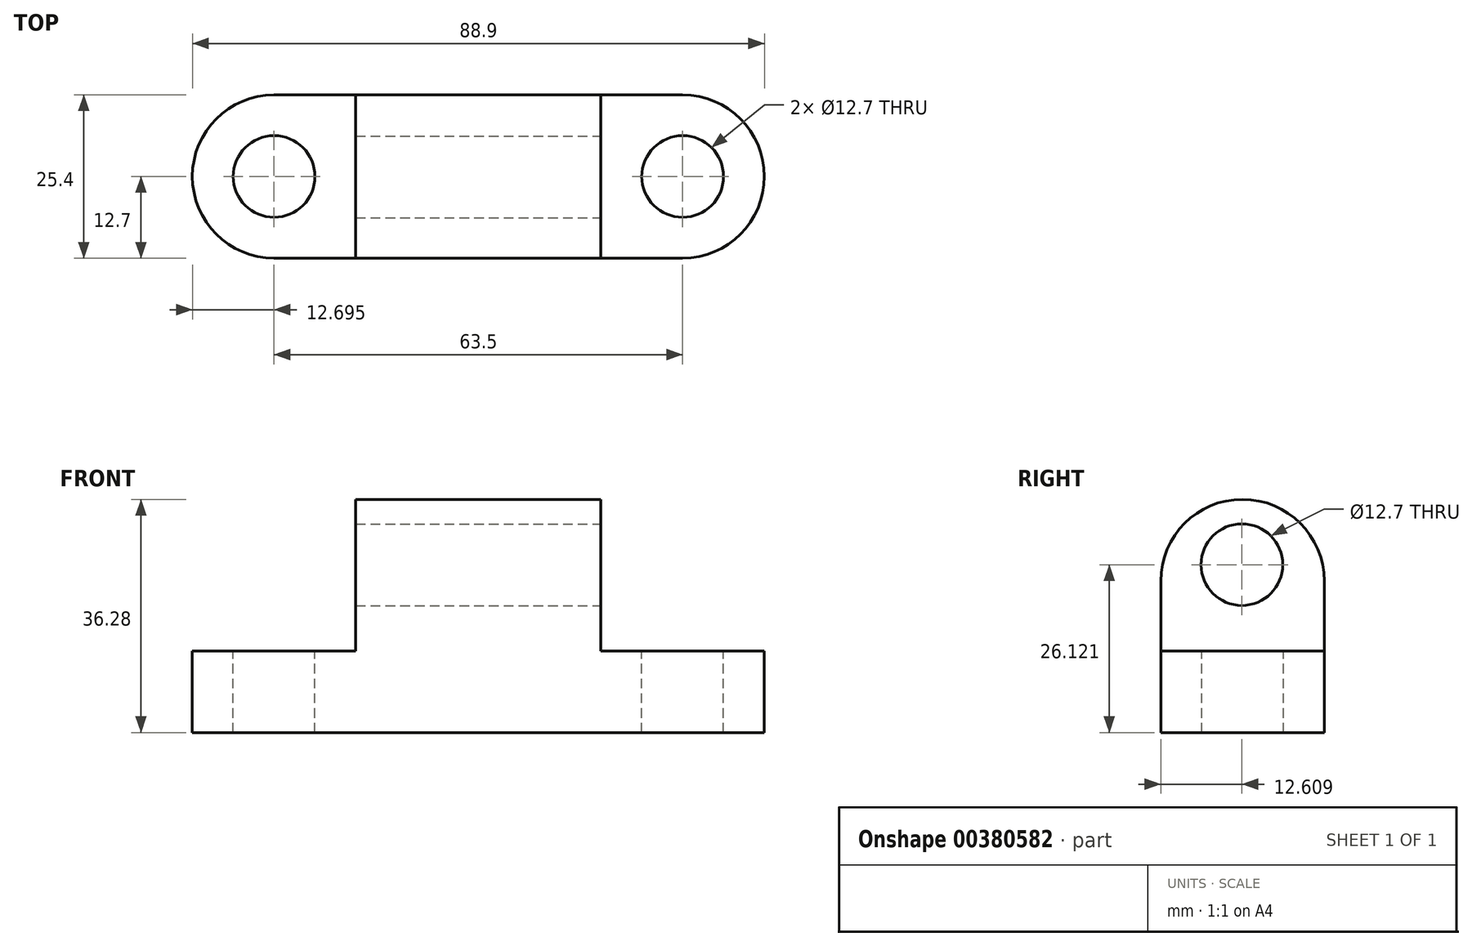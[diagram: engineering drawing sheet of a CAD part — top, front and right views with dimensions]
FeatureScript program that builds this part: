
annotation { "Feature Type Name" : "Feature", "Feature Type Description" : "" }
export const myFeature = defineFeature(function(context is Context, id is Id, definition is map)
    precondition{}
    {
        {
            var Q0;
            Q0=qCreatedBy(makeId("Front.planeOp"),FACE);
            var sketch = newSketch(context, id + "F0", { "sketchPlane" : qUnion([Q0])});
            skLineSegment(sketch, "E0", {"start": v(-50.93, 0) * mm, "end": v(-50.93, 12.7) * mm});
            skLineSegment(sketch, "E1", {"start": v(-50.93, 12.7) * mm, "end": v(-25.53, 12.7) * mm});
            skLineSegment(sketch, "E2", {"start": v(-25.53, 12.7) * mm, "end": v(-25.53, 36.28) * mm});
            skLineSegment(sketch, "E3", {"start": v(-25.53, 36.28) * mm, "end": v(12.57, 36.28) * mm});
            skLineSegment(sketch, "E4", {"start": v(12.57, 36.28) * mm, "end": v(12.57, 12.7) * mm});
            skLineSegment(sketch, "E5", {"start": v(12.57, 12.7) * mm, "end": v(37.97, 12.7) * mm});
            skLineSegment(sketch, "E6", {"start": v(37.97, 12.7) * mm, "end": v(37.97, 0) * mm});
            skLineSegment(sketch, "E7", {"start": v(37.97, 0) * mm, "end": v(-50.93, 0) * mm});
            skSolve(sketch);
        }
        {
            var Q0;
            Q0=makeQuery(id+"F0.imprint","IMPRINT",FACE,{"disambiguationData":[TD([[makeQuery(id+"F0.imprint","IMPRINT",EDGE,{"derivedFrom":sQuery(id+"F0.wireOp",EDGE,"E0")}),-1.0]])]});
            extrude(context, id + "F1", {"entities" : qUnion([Q0]), "depth" : 25.4 * mm});
        }
        {
            var Q0;
            Q0=makeQuery(id+"F1.opExtrude","SWEPT_FACE",FACE,{"disambiguationData":[OSD([sQuery(id+"F0.wireOp",EDGE,"E1")])]});
            var sketch = newSketch(context, id + "F2", { "sketchPlane" : qUnion([Q0])});
            skCircle(sketch, "E8", {"center": v(-38.23, -12.7) * mm, "radius": 12.7 * mm});
            skSolve(sketch);
        }
        {
            var Q0;
            {var subQ0=sQuery(id+"F2.wireOp",EDGE,"E8");var subQ1=sQuery(id+"F0.wireOp",EDGE,"E1");var subQ2=makeQuery(id+"F1.opExtrude","CAP_EDGE",EDGE,{"disambiguationData":[OSD([subQ1])],"isStart":true});var subQ3=makeQuery(id+"F2.imprint","INTERSECT",VERTEX,{"derivedFrom":[subQ2,subQ0]});Q0=makeQuery(id+"F2.imprint","IMPRINT",FACE,{"disambiguationData":[TD([[makeQuery(id+"F2.imprint","IMPRINT",EDGE,{"disambiguationData":[TD([[subQ3,-1.0]])],"derivedFrom":subQ0}),-1.0]])]});}
            var Q1;
            {var subQ0=sQuery(id+"F2.wireOp",EDGE,"E8");var subQ1=sQuery(id+"F0.wireOp",EDGE,"E1");var subQ4=makeQuery(id+"F1.opExtrude","CAP_EDGE",EDGE,{"disambiguationData":[OSD([subQ1])],"isStart":false});var subQ5=makeQuery(id+"F2.imprint","INTERSECT",VERTEX,{"derivedFrom":[subQ4,subQ0]});Q1=makeQuery(id+"F2.imprint","IMPRINT",FACE,{"disambiguationData":[TD([[makeQuery(id+"F2.imprint","IMPRINT",EDGE,{"disambiguationData":[TD([[subQ5,1.0]])],"derivedFrom":subQ0}),-1.0]])]});}
            extrude(context, id + "F3", {"entities" : qUnion([Q0, Q1]), "operationType" : NewBodyOperationType.REMOVE, "oppositeDirection" : true, "depth" : 25.4 * mm});
        }
        {
            var Q0;
            Q0=makeQuery(id+"F1.opExtrude","SWEPT_FACE",FACE,{"disambiguationData":[OSD([sQuery(id+"F0.wireOp",EDGE,"E5")])]});
            var sketch = newSketch(context, id + "F4", { "sketchPlane" : qUnion([Q0])});
            skCircle(sketch, "E9", {"center": v(25.27, -12.7) * mm, "radius": 12.7 * mm});
            skSolve(sketch);
        }
        {
            var Q0;
            {var subQ0=sQuery(id+"F4.wireOp",EDGE,"E9");var subQ1=sQuery(id+"F0.wireOp",EDGE,"E5");var subQ2=makeQuery(id+"F1.opExtrude","CAP_EDGE",EDGE,{"disambiguationData":[OSD([subQ1])],"isStart":true});var subQ3=makeQuery(id+"F4.imprint","INTERSECT",VERTEX,{"derivedFrom":[subQ2,subQ0]});Q0=makeQuery(id+"F4.imprint","IMPRINT",FACE,{"disambiguationData":[TD([[makeQuery(id+"F4.imprint","IMPRINT",EDGE,{"disambiguationData":[TD([[subQ3,1.0]])],"derivedFrom":subQ0}),-1.0]])]});}
            var Q1;
            {var subQ0=sQuery(id+"F4.wireOp",EDGE,"E9");var subQ1=sQuery(id+"F0.wireOp",EDGE,"E5");var subQ4=makeQuery(id+"F1.opExtrude","CAP_EDGE",EDGE,{"disambiguationData":[OSD([subQ1])],"isStart":false});var subQ5=makeQuery(id+"F4.imprint","INTERSECT",VERTEX,{"derivedFrom":[subQ4,subQ0]});Q1=makeQuery(id+"F4.imprint","IMPRINT",FACE,{"disambiguationData":[TD([[makeQuery(id+"F4.imprint","IMPRINT",EDGE,{"disambiguationData":[TD([[subQ5,-1.0]])],"derivedFrom":subQ0}),-1.0]])]});}
            extrude(context, id + "F5", {"entities" : qUnion([Q0, Q1]), "operationType" : NewBodyOperationType.REMOVE, "oppositeDirection" : true, "depth" : 25.4 * mm});
        }
        {
            var Q0;
            Q0=makeQuery(id+"F1.opExtrude","SWEPT_FACE",FACE,{"disambiguationData":[OSD([sQuery(id+"F0.wireOp",EDGE,"E1")])]});
            var sketch = newSketch(context, id + "F6", { "sketchPlane" : qUnion([Q0])});
            skCircle(sketch, "E10", {"center": v(-38.23, -12.7) * mm, "radius": 6.35 * mm});
            skSolve(sketch);
        }
        {
            var Q0;
            Q0=makeQuery(id+"F6.imprint","IMPRINT",FACE,{"disambiguationData":[TD([[makeQuery(id+"F6.imprint","IMPRINT",EDGE,{"derivedFrom":sQuery(id+"F6.wireOp",EDGE,"E10")}),1.0]])]});
            extrude(context, id + "F7", {"entities" : qUnion([Q0]), "operationType" : NewBodyOperationType.REMOVE, "oppositeDirection" : true, "depth" : 25.4 * mm});
        }
        {
            var Q0;
            Q0=makeQuery(id+"F1.opExtrude","SWEPT_FACE",FACE,{"disambiguationData":[OSD([sQuery(id+"F0.wireOp",EDGE,"E5")])]});
            var sketch = newSketch(context, id + "F8", { "sketchPlane" : qUnion([Q0])});
            skCircle(sketch, "E11", {"center": v(25.27, -12.7) * mm, "radius": 6.35 * mm});
            skSolve(sketch);
        }
        {
            var Q0;
            Q0=makeQuery(id+"F8.imprint","IMPRINT",FACE,{"disambiguationData":[TD([[makeQuery(id+"F8.imprint","IMPRINT",EDGE,{"derivedFrom":sQuery(id+"F8.wireOp",EDGE,"E11")}),1.0]])]});
            extrude(context, id + "F9", {"entities" : qUnion([Q0]), "operationType" : NewBodyOperationType.REMOVE, "oppositeDirection" : true, "depth" : 25.4 * mm});
        }
        {
            var Q0;
            Q0=makeQuery(id+"F1.opExtrude","SWEPT_FACE",FACE,{"disambiguationData":[OSD([sQuery(id+"F0.wireOp",EDGE,"E4")])]});
            var sketch = newSketch(context, id + "F10", { "sketchPlane" : qUnion([Q0])});
            skCircle(sketch, "E12", {"center": v(-12.8, 26.12) * mm, "radius": 6.35 * mm});
            skSolve(sketch);
        }
        {
            var Q0;
            Q0=makeQuery(id+"F10.imprint","IMPRINT",FACE,{"disambiguationData":[TD([[makeQuery(id+"F10.imprint","IMPRINT",EDGE,{"derivedFrom":sQuery(id+"F10.wireOp",EDGE,"E12")}),1.0]])]});
            extrude(context, id + "F11", {"entities" : qUnion([Q0]), "operationType" : NewBodyOperationType.REMOVE, "oppositeDirection" : true, "depth" : 38.1 * mm});
        }
        {
            var Q0;
            Q0=makeQuery(id+"F1.opExtrude","SWEPT_FACE",FACE,{"disambiguationData":[OSD([sQuery(id+"F0.wireOp",EDGE,"E4")])]});
            var sketch = newSketch(context, id + "F12", { "sketchPlane" : qUnion([Q0])});
            skCircle(sketch, "E13", {"center": v(-12.7, 23.58) * mm, "radius": 12.7 * mm});
            skSolve(sketch);
        }
        {
            var Q0;
            {var subQ0=sQuery(id+"F12.wireOp",EDGE,"E13");var subQ1=sQuery(id+"F0.wireOp",EDGE,"E4");var subQ4=makeQuery(id+"F1.opExtrude","CAP_EDGE",EDGE,{"disambiguationData":[OSD([subQ1])],"isStart":false});var subQ5=makeQuery(id+"F12.imprint","INTERSECT",VERTEX,{"derivedFrom":[subQ4,subQ0]});Q0=makeQuery(id+"F12.imprint","IMPRINT",FACE,{"disambiguationData":[TD([[makeQuery(id+"F12.imprint","IMPRINT",EDGE,{"disambiguationData":[TD([[subQ5,1.0]])],"derivedFrom":subQ0}),-1.0]])]});}
            var Q1;
            {var subQ0=sQuery(id+"F12.wireOp",EDGE,"E13");var subQ1=sQuery(id+"F0.wireOp",EDGE,"E4");var subQ4=makeQuery(id+"F1.opExtrude","CAP_EDGE",EDGE,{"disambiguationData":[OSD([subQ1])],"isStart":true});var subQ5=makeQuery(id+"F12.imprint","INTERSECT",VERTEX,{"derivedFrom":[subQ4,subQ0]});Q1=makeQuery(id+"F12.imprint","IMPRINT",FACE,{"disambiguationData":[TD([[makeQuery(id+"F12.imprint","IMPRINT",EDGE,{"disambiguationData":[TD([[subQ5,-1.0]])],"derivedFrom":subQ0}),-1.0]])]});}
            extrude(context, id + "F13", {"entities" : qUnion([Q0, Q1]), "operationType" : NewBodyOperationType.REMOVE, "oppositeDirection" : true, "depth" : 38.1 * mm});
        }
    });
